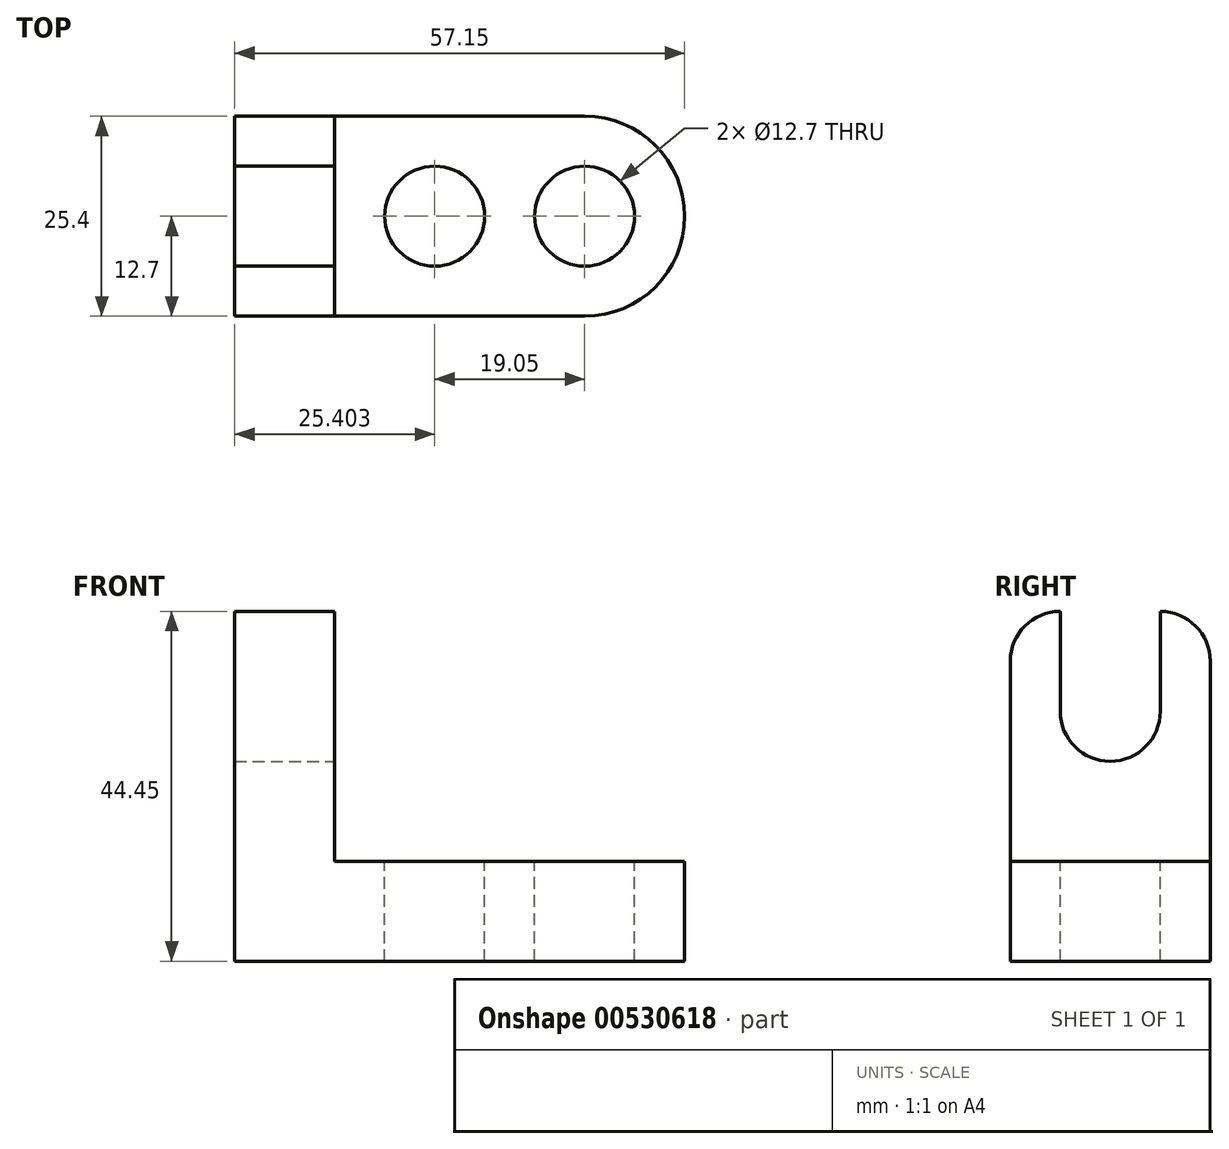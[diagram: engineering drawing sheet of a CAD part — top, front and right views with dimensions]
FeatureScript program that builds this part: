
annotation { "Feature Type Name" : "Feature", "Feature Type Description" : "" }
export const myFeature = defineFeature(function(context is Context, id is Id, definition is map)
    precondition{}
    {
        {
            var Q0;
            Q0=qCreatedBy(makeId("Front.planeOp"),FACE);
            var sketch = newSketch(context, id + "F0", { "sketchPlane" : qUnion([Q0])});
            skLineSegment(sketch, "E0", {"start": v(-60.72, 28.37) * mm, "end": v(-60.72, 15.67) * mm});
            skLineSegment(sketch, "E1", {"start": v(-60.72, 15.67) * mm, "end": v(-3.57, 15.67) * mm});
            skLineSegment(sketch, "E2", {"start": v(-3.57, 15.67) * mm, "end": v(-3.57, 28.37) * mm});
            skLineSegment(sketch, "E3", {"start": v(-3.57, 28.37) * mm, "end": v(-60.72, 28.37) * mm});
            skSolve(sketch);
        }
        {
            var Q0;
            Q0=makeQuery(id+"F0.imprint","IMPRINT",FACE,{"disambiguationData":[TD([[makeQuery(id+"F0.imprint","IMPRINT",EDGE,{"derivedFrom":sQuery(id+"F0.wireOp",EDGE,"E0")}),1.0]])]});
            extrude(context, id + "F1", {"entities" : qUnion([Q0]), "depth" : 25.4 * mm, "offsetDistance" : 25.4 * mm});
        }
        {
            var Q0;
            Q0=makeQuery(id+"F1.opExtrude","SWEPT_FACE",FACE,{"disambiguationData":[OSD([sQuery(id+"F0.wireOp",EDGE,"E3")])]});
            var sketch = newSketch(context, id + "F2", { "sketchPlane" : qUnion([Q0])});
            skLineSegment(sketch, "E4", {"start": v(-60.72, 0) * mm, "end": v(-60.72, -25.4) * mm});
            skLineSegment(sketch, "E5", {"start": v(-60.72, -25.4) * mm, "end": v(-48.02, -25.4) * mm});
            skLineSegment(sketch, "E6", {"start": v(-48.02, -25.4) * mm, "end": v(-48.02, 0) * mm});
            skLineSegment(sketch, "E7", {"start": v(-48.02, 0) * mm, "end": v(-60.72, 0) * mm});
            skSolve(sketch);
        }
        {
            var Q0;
            Q0=makeQuery(id+"F2.imprint","IMPRINT",FACE,{"disambiguationData":[TD([[makeQuery(id+"F2.imprint","IMPRINT",EDGE,{"derivedFrom":sQuery(id+"F2.wireOp",EDGE,"E4")}),-1.0]])]});
            extrude(context, id + "F3", {"entities" : qUnion([Q0]), "operationType" : NewBodyOperationType.ADD, "depth" : 31.75 * mm, "offsetDistance" : 25.4 * mm});
        }
        {
            var Q0;
            Q0=makeQuery(id+"F1.opExtrude","SWEPT_FACE",FACE,{"disambiguationData":[OSD([sQuery(id+"F0.wireOp",EDGE,"E3")])]});
            var sketch = newSketch(context, id + "F4", { "sketchPlane" : qUnion([Q0])});
            skCircle(sketch, "E8", {"center": v(-35.32, -12.7) * mm, "radius": 6.35 * mm});
            skCircle(sketch, "E9", {"center": v(-16.27, -12.7) * mm, "radius": 6.35 * mm});
            skSolve(sketch);
        }
        {
            var Q0;
            Q0=makeQuery(id+"F4.imprint","IMPRINT",FACE,{"disambiguationData":[TD([[makeQuery(id+"F4.imprint","IMPRINT",EDGE,{"derivedFrom":sQuery(id+"F4.wireOp",EDGE,"E9")}),1.0]])]});
            var Q1;
            Q1=makeQuery(id+"F4.imprint","IMPRINT",FACE,{"disambiguationData":[TD([[makeQuery(id+"F4.imprint","IMPRINT",EDGE,{"derivedFrom":sQuery(id+"F4.wireOp",EDGE,"E8")}),1.0]])]});
            extrude(context, id + "F5", {"entities" : qUnion([Q0, Q1]), "operationType" : NewBodyOperationType.REMOVE, "endBound" : BoundingType.THROUGH_ALL, "oppositeDirection" : true, "depth" : 25.4 * mm, "offsetDistance" : 25.4 * mm});
        }
        {
            var Q0;
            Q0=makeQuery(id+"F1.opExtrude","SWEPT_FACE",FACE,{"disambiguationData":[OSD([sQuery(id+"F0.wireOp",EDGE,"E3")])]});
            var sketch = newSketch(context, id + "F6", { "sketchPlane" : qUnion([Q0])});
            skCircle(sketch, "E10", {"center": v(-16.27, -12.7) * mm, "radius": 6.35 * mm});
            skCircle(sketch, "E11", {"center": v(-16.27, -12.7) * mm, "radius": 12.7 * mm});
            skSolve(sketch);
        }
        {
            var Q0;
            {var subQ0=sQuery(id+"F6.wireOp",EDGE,"E11");var subQ1=sQuery(id+"F0.wireOp",EDGE,"E3");var subQ4=makeQuery(id+"F1.opExtrude","CAP_EDGE",EDGE,{"disambiguationData":[OSD([subQ1])],"isStart":false});var subQ5=makeQuery(id+"F6.imprint","INTERSECT",VERTEX,{"derivedFrom":[subQ4,subQ0]});Q0=makeQuery(id+"F6.imprint","IMPRINT",FACE,{"disambiguationData":[TD([[makeQuery(id+"F6.imprint","IMPRINT",EDGE,{"disambiguationData":[TD([[subQ5,-1.0]])],"derivedFrom":subQ0}),-1.0]])]});}
            var Q1;
            {var subQ0=sQuery(id+"F6.wireOp",EDGE,"E11");var subQ1=sQuery(id+"F0.wireOp",EDGE,"E3");var subQ2=makeQuery(id+"F1.opExtrude","CAP_EDGE",EDGE,{"disambiguationData":[OSD([subQ1])],"isStart":true});var subQ3=makeQuery(id+"F6.imprint","INTERSECT",VERTEX,{"derivedFrom":[subQ2,subQ0]});Q1=makeQuery(id+"F6.imprint","IMPRINT",FACE,{"disambiguationData":[TD([[makeQuery(id+"F6.imprint","IMPRINT",EDGE,{"disambiguationData":[TD([[subQ3,1.0]])],"derivedFrom":subQ0}),-1.0]])]});}
            extrude(context, id + "F7", {"entities" : qUnion([Q0, Q1]), "operationType" : NewBodyOperationType.REMOVE, "oppositeDirection" : true, "depth" : 25.4 * mm, "offsetDistance" : 25.4 * mm});
        }
        {
            var Q0;
            Q0=makeQuery(id+"F3.opExtrude","SWEPT_FACE",FACE,{"disambiguationData":[OSD([sQuery(id+"F2.wireOp",EDGE,"E6")])]});
            var sketch = newSketch(context, id + "F8", { "sketchPlane" : qUnion([Q0])});
            skLineSegment(sketch, "E12", {"start": v(-25.4, 60.12) * mm, "end": v(-19.05, 60.12) * mm});
            skLineSegment(sketch, "E13", {"start": v(0, 60.12) * mm, "end": v(-6.35, 60.12) * mm});
            skLineSegment(sketch, "E14", {"start": v(-25.4, 28.37) * mm, "end": v(-25.4, 47.42) * mm});
            skLineSegment(sketch, "E15", {"start": v(0, 47.42) * mm, "end": v(0, 28.37) * mm});
            skLineSegment(sketch, "E16", {"start": v(0, 28.37) * mm, "end": v(0, 47.42) * mm});
            skLineSegment(sketch, "E17", {"start": v(-25.4, 47.42) * mm, "end": v(0, 47.42) * mm});
            skCircle(sketch, "E18", {"center": v(-12.7, 47.42) * mm, "radius": 6.35 * mm});
            skLineSegment(sketch, "E19", {"start": v(-19.05, 60.12) * mm, "end": v(-19.05, 47.42) * mm});
            skLineSegment(sketch, "E20", {"start": v(-6.35, 60.12) * mm, "end": v(-6.35, 47.42) * mm});
            skPoint(sketch, "E21.startSnap0", {"position": v(-22.23, 60.12) * mm});
            skLineSegment(sketch, "E22", {"start": v(-25.4, 60.12) * mm, "end": v(-25.4, 53.77) * mm});
            skLineSegment(sketch, "E23", {"start": v(0, 60.12) * mm, "end": v(0, 53.77) * mm});
            skArc(sketch, "E24", {"start": v(-19.05, 60.12) * mm, "mid": v(-23.54, 58.26) * mm, "end": v(-25.4, 53.77) * mm});
            skArc(sketch, "E25", {"start": v(0, 53.77) * mm, "mid": v(-1.86, 58.26) * mm, "end": v(-6.35, 60.12) * mm});
            skSolve(sketch);
        }
        {
            var Q0;
            {var subQ0=sQuery(id+"F8.wireOp",EDGE,"E19");Q0=makeQuery(id+"F8.imprint","IMPRINT",FACE,{"disambiguationData":[TD([[makeQuery(id+"F8.imprint","IMPRINT",EDGE,{"derivedFrom":subQ0}),1.0]])]});}
            var Q1;
            {var subQ0=sQuery(id+"F8.wireOp",EDGE,"E18");var subQ1=sQuery(id+"F8.wireOp",EDGE,"E17");var subQ2=makeQuery(id+"F8.imprint","INTERSECT",VERTEX,{"derivedFrom":[subQ1,subQ0,sQuery(id+"F8.wireOp",EDGE,"E19")]});Q1=makeQuery(id+"F8.imprint","IMPRINT",FACE,{"disambiguationData":[TD([[makeQuery(id+"F8.imprint","IMPRINT",EDGE,{"disambiguationData":[TD([[subQ2,-1.0]])],"derivedFrom":subQ1}),1.0]])]});}
            var Q2;
            {var subQ0=sQuery(id+"F8.wireOp",EDGE,"E18");var subQ1=sQuery(id+"F8.wireOp",EDGE,"E17");var subQ2=makeQuery(id+"F8.imprint","INTERSECT",VERTEX,{"derivedFrom":[subQ1,subQ0,sQuery(id+"F8.wireOp",EDGE,"E19")]});Q2=makeQuery(id+"F8.imprint","IMPRINT",FACE,{"disambiguationData":[TD([[makeQuery(id+"F8.imprint","IMPRINT",EDGE,{"disambiguationData":[TD([[subQ2,-1.0]])],"derivedFrom":subQ1}),-1.0]])]});}
            extrude(context, id + "F9", {"entities" : qUnion([Q0, Q1, Q2]), "operationType" : NewBodyOperationType.REMOVE, "endBound" : BoundingType.THROUGH_ALL, "oppositeDirection" : true, "depth" : 25.4 * mm, "offsetDistance" : 25.4 * mm});
        }
        {
            var Q0;
            Q0=makeQuery(id+"F3.opExtrude","SWEPT_FACE",FACE,{"disambiguationData":[OSD([sQuery(id+"F2.wireOp",EDGE,"E6")])]});
            extrude(context, id + "F10", {"entities" : qUnion([Q0]), "operationType" : NewBodyOperationType.REMOVE, "depth" : 25.4 * mm, "offsetDistance" : 25.4 * mm});
        }
        {
            var Q0;
            Q0=makeQuery(id+"F3.opExtrude","SWEPT_FACE",FACE,{"disambiguationData":[OSD([sQuery(id+"F2.wireOp",EDGE,"E6")])]});
            var sketch = newSketch(context, id + "F11", { "sketchPlane" : qUnion([Q0])});
            skLineSegment(sketch, "E26", {"start": v(-25.4, 60.12) * mm, "end": v(-25.4, 53.77) * mm});
            skLineSegment(sketch, "E27", {"start": v(0, 60.12) * mm, "end": v(0, 53.77) * mm});
            skArc(sketch, "E28", {"start": v(-19.05, 60.12) * mm, "mid": v(-23.54, 58.26) * mm, "end": v(-25.4, 53.77) * mm});
            skArc(sketch, "E29", {"start": v(0, 53.77) * mm, "mid": v(-1.86, 58.26) * mm, "end": v(-6.35, 60.12) * mm});
            skSolve(sketch);
        }
        {
            var Q0;
            Q0=makeQuery(id+"F11.imprint","IMPRINT",FACE,{"disambiguationData":[TD([[makeQuery(id+"F11.imprint","IMPRINT",EDGE,{"derivedFrom":sQuery(id+"F11.wireOp",EDGE,"E26")}),1.0]])]});
            var Q1;
            Q1=makeQuery(id+"F11.imprint","IMPRINT",FACE,{"disambiguationData":[TD([[makeQuery(id+"F11.imprint","IMPRINT",EDGE,{"derivedFrom":sQuery(id+"F11.wireOp",EDGE,"E27")}),-1.0]])]});
            extrude(context, id + "F12", {"entities" : qUnion([Q0, Q1]), "operationType" : NewBodyOperationType.REMOVE, "endBound" : BoundingType.THROUGH_ALL, "oppositeDirection" : true, "depth" : 25.4 * mm, "offsetDistance" : 25.4 * mm});
        }
    });
